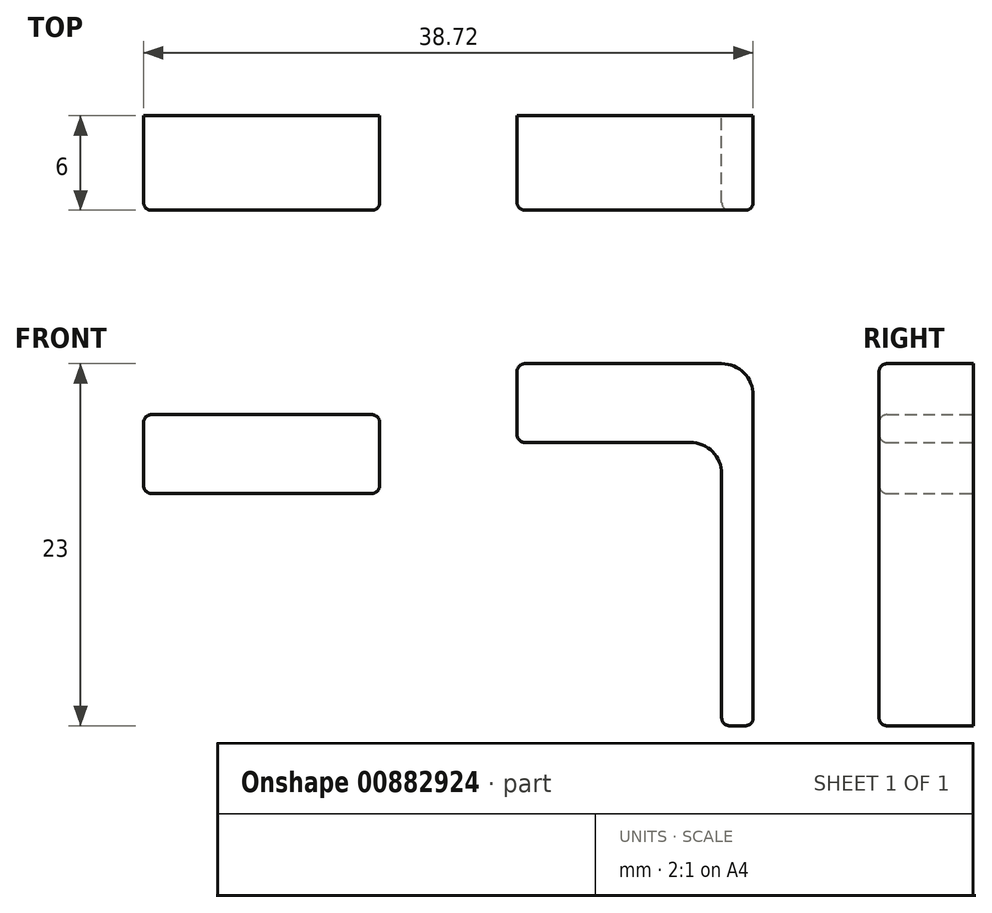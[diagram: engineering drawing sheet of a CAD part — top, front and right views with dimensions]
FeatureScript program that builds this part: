
annotation { "Feature Type Name" : "Feature", "Feature Type Description" : "" }
export const myFeature = defineFeature(function(context is Context, id is Id, definition is map)
    precondition{}
    {
        {
            var Q0;
            Q0=qCreatedBy(makeId("Front.planeOp"),FACE);
            var sketch = newSketch(context, id + "F0", { "sketchPlane" : qUnion([Q0])});
            skLineSegment(sketch, "E0", {"start": v(0, 18) * mm, "end": v(13, 18) * mm});
            skLineSegment(sketch, "E1", {"start": v(13, 18) * mm, "end": v(13, 0) * mm});
            skLineSegment(sketch, "E2", {"start": v(13, 0) * mm, "end": v(15, 0) * mm});
            skLineSegment(sketch, "E3", {"start": v(15, 0) * mm, "end": v(15, 23) * mm});
            skLineSegment(sketch, "E4", {"start": v(15, 23) * mm, "end": v(0, 23) * mm});
            skLineSegment(sketch, "E5", {"start": v(0, 23) * mm, "end": v(0, 18) * mm});
            skLineSegment(sketch, "E6.bottom", {"start": v(-23.72, 19.76) * mm, "end": v(-8.72, 19.76) * mm});
            skLineSegment(sketch, "E6.top", {"start": v(-23.72, 14.76) * mm, "end": v(-8.72, 14.76) * mm});
            skLineSegment(sketch, "E6.left", {"start": v(-23.72, 19.76) * mm, "end": v(-23.72, 14.76) * mm});
            skLineSegment(sketch, "E6.right", {"start": v(-8.72, 19.76) * mm, "end": v(-8.72, 14.76) * mm});
            skSolve(sketch);
        }
        {
            var Q0;
            Q0 = qSketchRegion(id + "F0", true);
            extrude(context, id + "F1", {"entities" : qUnion([Q0]), "depth" : 6 * mm, "offsetDistance" : 25 * mm});
        }
        {
            var Q0;
            Q0=makeQuery(id+"F1.opExtrude","SWEPT_EDGE",EDGE,{"disambiguationData":[OSD([sQuery(id+"F0.wireOp",EDGE,"E3"),sQuery(id+"F0.wireOp",EDGE,"E4")])]});
            var Q1;
            Q1=makeQuery(id+"F1.opExtrude","SWEPT_EDGE",EDGE,{"disambiguationData":[OSD([sQuery(id+"F0.wireOp",EDGE,"E0"),sQuery(id+"F0.wireOp",EDGE,"E1")])]});
            fillet(context, id + "F2", {"entities" : qUnion([Q0, Q1]), "radius" : 2 * mm, "tangentPropagation" : true, "allowEdgeOverflow" : false});
        }
        {
            var Q0;
            Q0=makeQuery(id+"F1.opExtrude","SWEPT_EDGE",EDGE,{"disambiguationData":[OSD([sQuery(id+"F0.wireOp",EDGE,"E4"),sQuery(id+"F0.wireOp",EDGE,"E5")])]});
            var Q1;
            Q1=makeQuery(id+"F1.opExtrude","SWEPT_EDGE",EDGE,{"disambiguationData":[OSD([sQuery(id+"F0.wireOp",EDGE,"E0"),sQuery(id+"F0.wireOp",EDGE,"E5")])]});
            var Q2;
            Q2=makeQuery(id+"F1.opExtrude","SWEPT_EDGE",EDGE,{"disambiguationData":[OSD([sQuery(id+"F0.wireOp",EDGE,"E1"),sQuery(id+"F0.wireOp",EDGE,"E2")])]});
            var Q3;
            Q3=makeQuery(id+"F1.opExtrude","SWEPT_EDGE",EDGE,{"disambiguationData":[OSD([sQuery(id+"F0.wireOp",EDGE,"E2"),sQuery(id+"F0.wireOp",EDGE,"E3")])]});
            var Q4;
            Q4=makeQuery(id+"F1.opExtrude","CAP_EDGE",EDGE,{"disambiguationData":[OSD([sQuery(id+"F0.wireOp",EDGE,"E1")])],"isStart":false});
            var Q5;
            Q5=makeQuery(id+"F1.opExtrude","CAP_EDGE",EDGE,{"disambiguationData":[OSD([sQuery(id+"F0.wireOp",EDGE,"E3")])],"isStart":false});
            var Q6;
            Q6=makeQuery(id+"F1.opExtrude","CAP_EDGE",EDGE,{"disambiguationData":[OSD([sQuery(id+"F0.wireOp",EDGE,"E6.top")])],"isStart":false});
            var Q7;
            Q7=makeQuery(id+"F1.opExtrude","CAP_EDGE",EDGE,{"disambiguationData":[OSD([sQuery(id+"F0.wireOp",EDGE,"E6.left")])],"isStart":false});
            var Q8;
            Q8=makeQuery(id+"F1.opExtrude","SWEPT_EDGE",EDGE,{"disambiguationData":[OSD([sQuery(id+"F0.wireOp",EDGE,"E6.top"),sQuery(id+"F0.wireOp",EDGE,"E6.left")])]});
            var Q9;
            Q9=makeQuery(id+"F1.opExtrude","SWEPT_EDGE",EDGE,{"disambiguationData":[OSD([sQuery(id+"F0.wireOp",EDGE,"E6.bottom"),sQuery(id+"F0.wireOp",EDGE,"E6.left")])]});
            var Q10;
            Q10=makeQuery(id+"F1.opExtrude","SWEPT_EDGE",EDGE,{"disambiguationData":[OSD([sQuery(id+"F0.wireOp",EDGE,"E6.top"),sQuery(id+"F0.wireOp",EDGE,"E6.right")])]});
            var Q11;
            Q11=makeQuery(id+"F1.opExtrude","CAP_EDGE",EDGE,{"disambiguationData":[OSD([sQuery(id+"F0.wireOp",EDGE,"E6.right")])],"isStart":false});
            var Q12;
            Q12=makeQuery(id+"F1.opExtrude","CAP_EDGE",EDGE,{"disambiguationData":[OSD([sQuery(id+"F0.wireOp",EDGE,"E6.bottom")])],"isStart":false});
            var Q13;
            Q13=makeQuery(id+"F1.opExtrude","SWEPT_EDGE",EDGE,{"disambiguationData":[OSD([sQuery(id+"F0.wireOp",EDGE,"E6.bottom"),sQuery(id+"F0.wireOp",EDGE,"E6.right")])]});
            var Q14;
            Q14=makeQuery(id+"F1.opExtrude","CAP_EDGE",EDGE,{"disambiguationData":[OSD([sQuery(id+"F0.wireOp",EDGE,"E5")])],"isStart":false});
            var Q15;
            Q15=makeQuery(id+"F1.opExtrude","CAP_EDGE",EDGE,{"disambiguationData":[OSD([sQuery(id+"F0.wireOp",EDGE,"E2")])],"isStart":false});
            fillet(context, id + "F3", {"entities" : qUnion([Q0, Q1, Q2, Q3, Q4, Q5, Q6, Q7, Q8, Q9, Q10, Q11, Q12, Q13, Q14, Q15]), "radius" : 0.5 * mm, "tangentPropagation" : true, "allowEdgeOverflow" : false});
        }
    });
